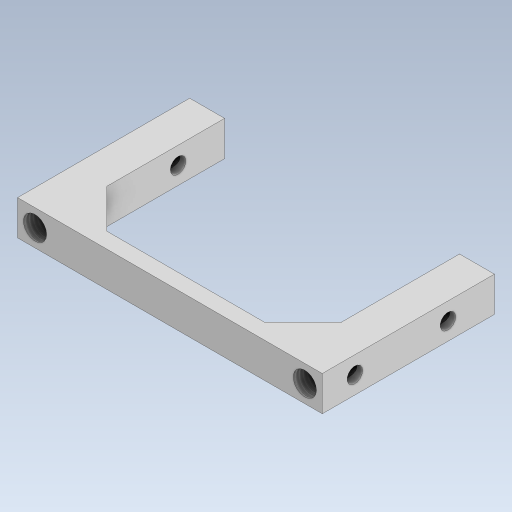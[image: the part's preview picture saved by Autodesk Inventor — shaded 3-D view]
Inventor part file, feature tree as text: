
AUTODESK INVENTOR PART (.ipt)
format: ipt  version: 2023.5 (Build 275446000, 446)  size: 167,936 bytes
history: native  units: in
note: dims shown in document units (in); Inventor stores cm internally (conversion verified against a paired STEP export)
features: extrude x6, sketch x5, plane x2, thread x2
ambient origin geometry x8: Origin, YZ Plane, XZ Plane, XY Plane, X Axis, Y Axis, Z Axis, Center Point
bodies: Solid1 (feature_tree)
feature tree (15):
  sketch  "Sketch1"  dims[d0=0.1181in d1=0.685in]
  extrude  "Extrusion1"  Depth=0.685in
  extrude  "Extrusion2"  Depth=0.1772in
  plane  "Work Plane1"
  extrude  "Extrusion3"  Depth=0.874in TaperAngle=0.0deg
  plane  "Work Plane2"
  extrude  "Extrusion4"  Depth=0.1969in
  extrude  "Extrusion5"  Depth=0.1969in
  thread  "Thread1"  [1 undecoded]
  thread  "Thread2"  [1 undecoded]
  extrude  "Extrusion6"  Depth=0.874in TaperAngle=0.0deg
  sketch  "Sketch2"  dims[d2=0.1772in d3=0.1772in]
  sketch  "Sketch5"  dims[d4=0.7953in d5=0.0in d6=0.874in d7=0.0in]
  sketch  "Sketch6"  dims[d8=0.0787in d9=0.0in d10=0.1969in]
  sketch  "Sketch7"  dims[d11=0.1969in d12=0.1969in d13=0.1772in d14=0.0in d15=0.0787in d16=0.0in d17=0.874in d18=0.0in d19=0.874in d20=0.0in d21=0.0787in d22=0.2362in d23=0.0787in d24=0.4724in d25=1.5748in d26=0.0in]
note: 2 required parameter values undecoded (feature->parameter linkage not recoverable at this tier; creation-order binding heuristic only, values carry confidence <= 0.55)
